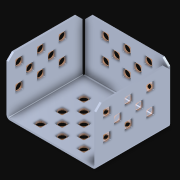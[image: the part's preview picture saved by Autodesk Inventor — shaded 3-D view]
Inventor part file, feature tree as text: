
AUTODESK INVENTOR PART (.ipt)
format: ipt  version: 2021 (Build 250183000, 183)  size: 627,200 bytes
history: native  units: in
note: dims shown in document units (in); Inventor stores cm internally (conversion verified against a paired STEP export)
features: other x38, extrude x37, pattern_linear x8, imported_body x1, sketch x1
ambient origin geometry x8: Origin, YZ Plane, XZ Plane, XY Plane, X Axis, Y Axis, Z Axis, Center Point
bodies: Body1 (feature_tree), Body2 (feature_tree), Body3 (feature_tree), Body4 (feature_tree), Body5 (feature_tree), Body6 (feature_tree), Body7 (feature_tree), Body8 (feature_tree), Body9 (feature_tree), Body10 (feature_tree), Body11 (feature_tree), Body12 (feature_tree), Body13 (feature_tree), Body14 (feature_tree), Body15 (feature_tree), Body16 (feature_tree), Body17 (feature_tree), Body18 (feature_tree), Body19 (feature_tree), Body20 (feature_tree), Body21 (feature_tree), Body22 (feature_tree), Body23 (feature_tree), Body24 (feature_tree), Body25 (feature_tree), Body26 (feature_tree), Body27 (feature_tree), Body28 (feature_tree), Body29 (feature_tree), Body30 (feature_tree), Body31 (feature_tree), Body32 (feature_tree), Body33 (feature_tree), Body34 (feature_tree), Body35 (feature_tree), Body36 (feature_tree), Body37 (feature_tree), Body38 (feature_tree)
feature tree (85):
  parser-record x1  (decoder bookkeeping rows leaked as tree rows — omitted from the tree; the rows remain in map.json)
  imported_body  "Base1"
  pattern_linear  "Rectangular Pattern1"  Count1=3 Spacing1=0.5in
  pattern_linear  "Rectangular Pattern2"  Count1=2 Spacing1=0.5in
  pattern_linear  "Rectangular Pattern3"  Spacing1=0.046in  [1 undecoded]
  pattern_linear  "Rectangular Pattern4"  Count1=2 Spacing1=0.5in
  pattern_linear  "Rectangular Pattern5"  Spacing1=0.046in  [1 undecoded]
  pattern_linear  "Rectangular Pattern6"  Count1=3 Spacing1=0.5in
  pattern_linear  "Rectangular Pattern7"  Count1=2 Spacing1=0.5in
  pattern_linear  "Rectangular Pattern8"  Spacing1=0.046in  [1 undecoded]
  other  "Srf1"
  other  "Srf2"
  other  "Srf3"
  other  "Srf4"
  other  "Srf5"
  other  "Srf6"
  other  "Srf7"
  other  "Srf8"
  other  "Srf9"
  other  "Srf10"
  other  "Srf11"
  other  "Srf12"
  other  "Srf13"
  other  "Srf14"
  other  "Srf15"
  other  "Srf16"
  other  "Srf17"
  other  "Srf18"
  other  "Srf19"
  other  "Srf20"
  other  "Srf21"
  other  "Srf22"
  other  "Srf23"
  other  "Srf24"
  other  "Srf25"
  other  "Srf26"
  other  "Srf27"
  other  "Srf28"
  other  "Srf29"
  other  "Srf30"
  other  "Srf31"
  other  "Srf32"
  other  "Srf33"
  sketch  "Sketch8"  dims[d118=0.046in d119=0.0in d120=1.1811in d122=0.5in d123=0.7874in d125=0.5in d127=0.046in d128=0.0in d129=0.7874in d131=0.5in d133=0.046in d134=0.0in d135=1.1811in d137=0.5in d138=0.7874in d140=0.5in d142=0.046in d143=0.0in d144=0.7874in d146=0.5in d148=0.046in d149=0.0in d150=1.1811in d152=0.5in d153=0.7874in d155=0.5in d157=0.046in d158=0.0in d159=0.7874in d161=0.5in d163=0.046in d164=0.0in d165=1.1811in d167=0.5in d168=1.1811in d170=0.5in d171=0.167in d172=0.046in d173=0.0in d174=0.7874in d176=0.5in d177=0.7874in d179=0.5in]
  other  "Srf34"
  other  "Srf35"
  other  "Srf36"
  other  "Srf37"
  extrude  "ExtrusionSrf1"  Depth=0.5in
  extrude  "ExtrusionSrf7"  Depth=0.046in TaperAngle=0.0deg
  extrude  "ExtrusionSrf9"  Depth=0.5in
  extrude  "ExtrusionSrf15"  Depth=0.5in
  extrude  "ExtrusionSrf17"  Depth=0.046in TaperAngle=0.0deg
  extrude  "ExtrusionSrf23"  Depth=0.5in
  extrude  "ExtrusionSrf25"  Depth=0.046in TaperAngle=0.0deg
  extrude  "ExtrusionSrf34"  Depth=0.5in
  extrude  "ExtrusionSrf2"  Depth=0.5in
  extrude  "ExtrusionSrf3"  Depth=0.5in
  extrude  "ExtrusionSrf4"  Depth=0.046in TaperAngle=0.0deg
  extrude  "ExtrusionSrf5"  Depth=0.5in
  extrude  "ExtrusionSrf6"  Depth=0.5in
  extrude  "ExtrusionSrf8"  [1 undecoded]
  extrude  "ExtrusionSrf10"  [1 undecoded]
  extrude  "ExtrusionSrf11"  [1 undecoded]
  extrude  "ExtrusionSrf12"  [1 undecoded]
  extrude  "ExtrusionSrf13"  [1 undecoded]
  extrude  "ExtrusionSrf14"  [1 undecoded]
  extrude  "ExtrusionSrf16"  [1 undecoded]
  extrude  "ExtrusionSrf18"  [1 undecoded]
  extrude  "ExtrusionSrf19"  [1 undecoded]
  extrude  "ExtrusionSrf20"  [1 undecoded]
  extrude  "ExtrusionSrf21"  [1 undecoded]
  extrude  "ExtrusionSrf22"  [1 undecoded]
  extrude  "ExtrusionSrf24"  [1 undecoded]
  extrude  "ExtrusionSrf26"  [1 undecoded]
  extrude  "ExtrusionSrf27"  [1 undecoded]
  extrude  "ExtrusionSrf28"  [1 undecoded]
  extrude  "ExtrusionSrf29"  [1 undecoded]
  extrude  "ExtrusionSrf30"  [1 undecoded]
  extrude  "ExtrusionSrf31"  [1 undecoded]
  extrude  "ExtrusionSrf32"  [1 undecoded]
  extrude  "ExtrusionSrf33"  [1 undecoded]
  extrude  "ExtrusionSrf35"  [1 undecoded]
  extrude  "ExtrusionSrf36"  [1 undecoded]
  extrude  "ExtrusionSrf37"  [1 undecoded]
note: 27 required parameter values undecoded (feature->parameter linkage not recoverable at this tier; creation-order binding heuristic only, values carry confidence <= 0.55)
